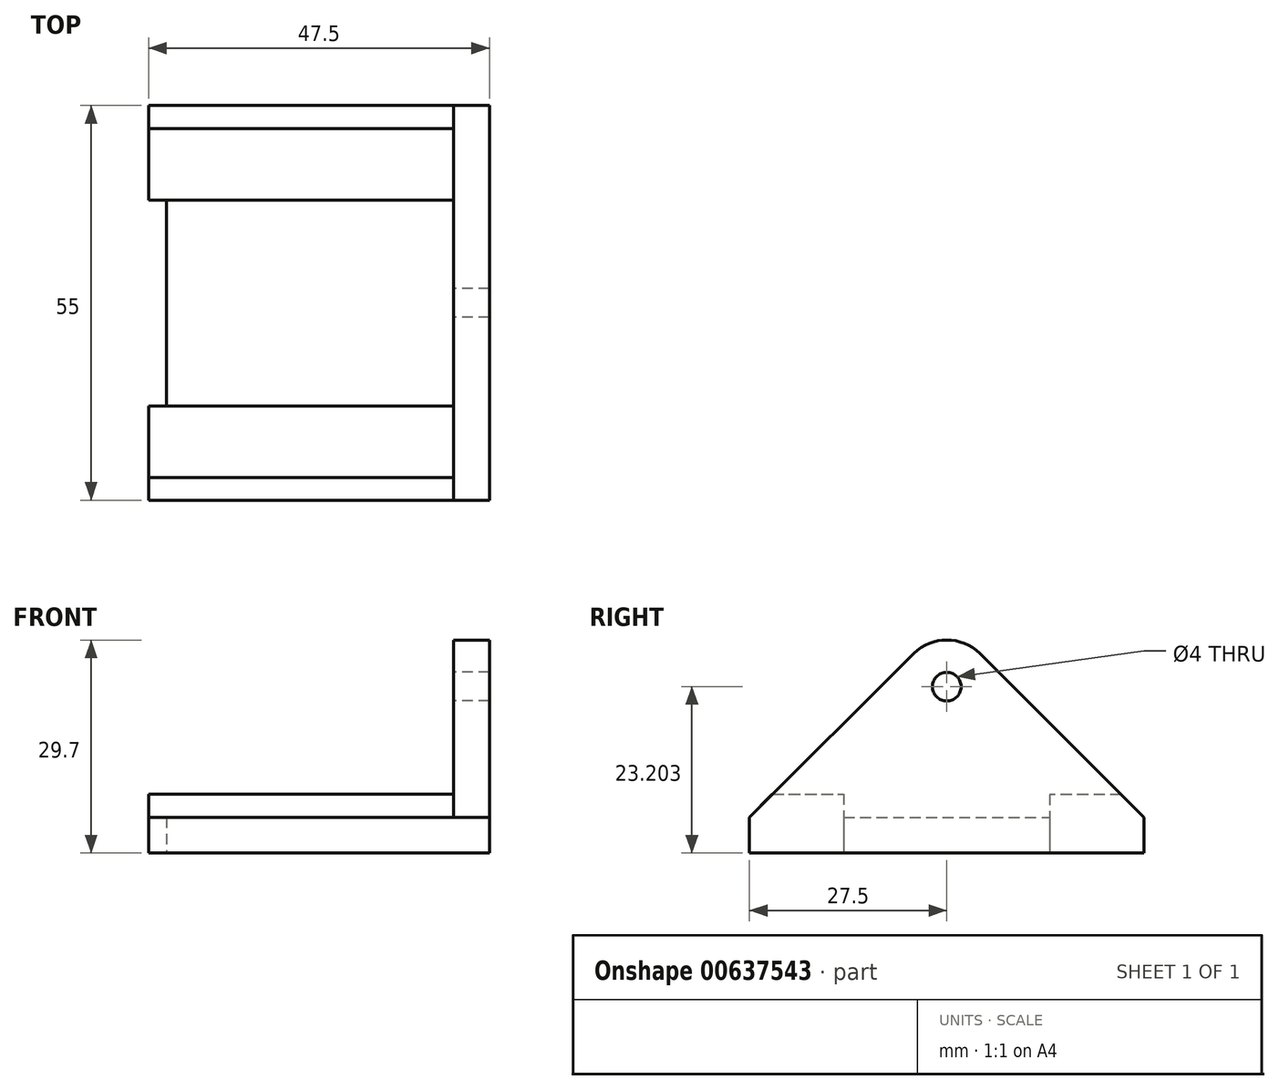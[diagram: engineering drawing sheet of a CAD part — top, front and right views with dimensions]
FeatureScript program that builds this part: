
annotation { "Feature Type Name" : "Feature", "Feature Type Description" : "" }
export const myFeature = defineFeature(function(context is Context, id is Id, definition is map)
    precondition{}
    {
        {
            var Q0;
            Q0=qCreatedBy(makeId("Front.planeOp"),FACE);
            var sketch = newSketch(context, id + "F0", { "sketchPlane" : qUnion([Q0])});
            skLineSegment(sketch, "E0.bottom", {"start": v(-40, 5) * mm, "end": v(0, 5) * mm});
            skLineSegment(sketch, "E0.top", {"start": v(-40, 0) * mm, "end": v(0, 0) * mm});
            skLineSegment(sketch, "E0.left", {"start": v(-40, 5) * mm, "end": v(-40, 0) * mm});
            skLineSegment(sketch, "E0.right", {"start": v(0, 5) * mm, "end": v(0, 0) * mm});
            skSolve(sketch);
        }
        {
            var Q0;
            Q0 = qSketchRegion(id + "F0", true);
            extrude(context, id + "F1", {"entities" : qUnion([Q0]), "depth" : 55 * mm, "offsetDistance" : 25 * mm});
        }
        {
            var Q0;
            Q0=qCreatedBy(makeId("Right.planeOp"),FACE);
            var sketch = newSketch(context, id + "F2", { "sketchPlane" : qUnion([Q0])});
            skLineSegment(sketch, "E1", {"start": v(0, 0) * mm, "end": v(-5.74, 0) * mm});
            skLineSegment(sketch, "E2", {"start": v(0, 0) * mm, "end": v(-55, 0) * mm});
            skLineSegment(sketch, "E3", {"start": v(0, 0) * mm, "end": v(0, 4.96) * mm});
            skLineSegment(sketch, "E4", {"start": v(0, 4.96) * mm, "end": v(-55, 4.96) * mm});
            skLineSegment(sketch, "E5", {"start": v(-55, 4.96) * mm, "end": v(-55, 0) * mm});
            skCircle(sketch, "E6", {"center": v(-27.5, 23.2) * mm, "radius": 2 * mm});
            skArc(sketch, "E7", {"start": v(-22.91, 27.8) * mm, "mid": v(-27.5, 29.7) * mm, "end": v(-32.09, 27.8) * mm});
            skLineSegment(sketch, "E8", {"start": v(0, 4.96) * mm, "end": v(-22.91, 27.8) * mm});
            skLineSegment(sketch, "E9", {"start": v(-32.09, 27.8) * mm, "end": v(-55, 4.96) * mm});
            skSolve(sketch);
        }
        {
            var Q0;
            Q0 = qSketchRegion(id + "F2", true);
            extrude(context, id + "F3", {"entities" : qUnion([Q0]), "operationType" : NewBodyOperationType.ADD, "depth" : 5 * mm, "offsetDistance" : 25 * mm});
        }
        {
            var Q0;
            Q0=qCreatedBy(makeId("Right.planeOp"),FACE);
            var sketch = newSketch(context, id + "F4", { "sketchPlane" : qUnion([Q0])});
            skLineSegment(sketch, "E10", {"start": v(-55, 0) * mm, "end": v(-55, 5) * mm});
            skLineSegment(sketch, "E11", {"start": v(0, 5) * mm, "end": v(0, 0) * mm});
            skLineSegment(sketch, "E12", {"start": v(0, 5) * mm, "end": v(-3.18, 8.18) * mm});
            skLineSegment(sketch, "E13", {"start": v(-3.18, 8.18) * mm, "end": v(-13.18, 8.18) * mm});
            skLineSegment(sketch, "E14", {"start": v(-13.18, 8.18) * mm, "end": v(-13.18, 0) * mm});
            skLineSegment(sketch, "E15", {"start": v(-13.18, 0) * mm, "end": v(0, 0) * mm});
            skLineSegment(sketch, "E16", {"start": v(-55, 5) * mm, "end": v(-51.87, 8.24) * mm});
            skLineSegment(sketch, "E17", {"start": v(-51.87, 8.24) * mm, "end": v(-41.87, 8.24) * mm});
            skLineSegment(sketch, "E18", {"start": v(-41.87, 8.24) * mm, "end": v(-41.87, 0) * mm});
            skLineSegment(sketch, "E19", {"start": v(-41.87, 0) * mm, "end": v(-55, 0) * mm});
            skSolve(sketch);
        }
        {
            var Q0;
            Q0 = qSketchRegion(id + "F4", true);
            extrude(context, id + "F5", {"entities" : qUnion([Q0]), "operationType" : NewBodyOperationType.ADD, "oppositeDirection" : true, "depth" : 42.5 * mm, "offsetDistance" : 25 * mm});
        }
    });
